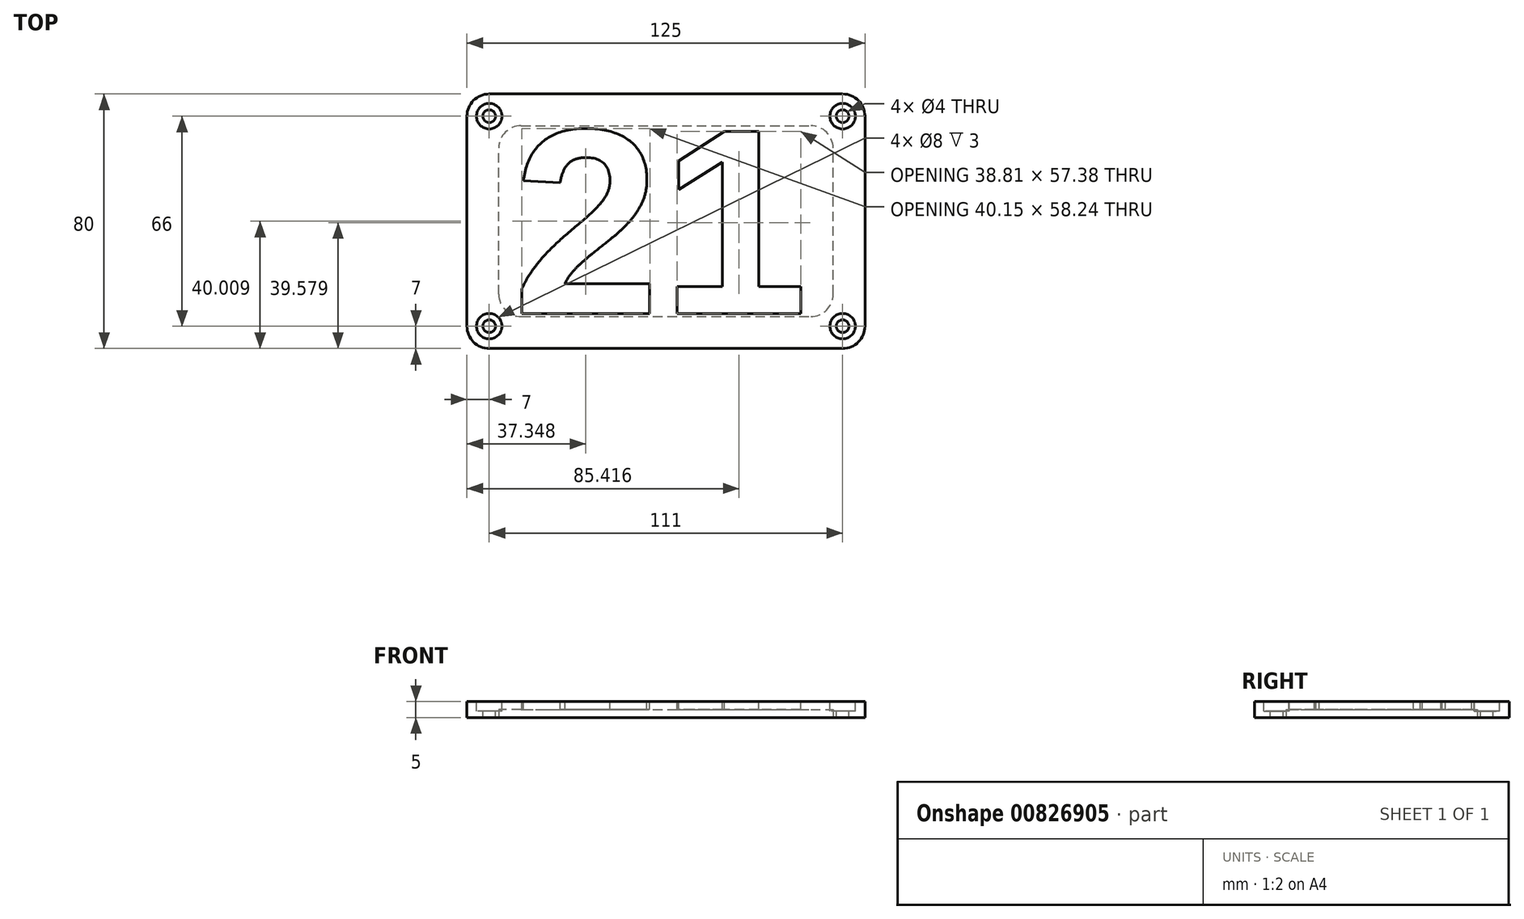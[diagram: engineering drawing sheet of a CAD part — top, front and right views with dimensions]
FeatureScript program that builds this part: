
annotation { "Feature Type Name" : "Feature", "Feature Type Description" : "" }
export const myFeature = defineFeature(function(context is Context, id is Id, definition is map)
    precondition{}
    {
        {
            var Q0;
            Q0=qCreatedBy(makeId("Top.planeOp"),FACE);
            var sketch = newSketch(context, id + "F0", { "sketchPlane" : qUnion([Q0])});
            skLineSegment(sketch, "E0.bottom", {"start": v(-62.5, 40) * mm, "end": v(62.5, 40) * mm});
            skLineSegment(sketch, "E0.top", {"start": v(-62.5, -40) * mm, "end": v(62.5, -40) * mm});
            skLineSegment(sketch, "E0.left", {"start": v(-62.5, 40) * mm, "end": v(-62.5, -40) * mm});
            skLineSegment(sketch, "E0.right", {"start": v(62.5, 40) * mm, "end": v(62.5, -40) * mm});
            skPoint(sketch, "E0.middle", {"position": v(0, 0) * mm});
            skSolve(sketch);
        }
        {
            var Q0;
            Q0=makeQuery(id+"F0.imprint","IMPRINT",FACE,{"disambiguationData":[TD([[makeQuery(id+"F0.imprint","IMPRINT",EDGE,{"derivedFrom":sQuery(id+"F0.wireOp",EDGE,"E0.bottom")}),-1.0]])]});
            extrude(context, id + "F1", {"entities" : qUnion([Q0]), "depth" : 5 * mm, "offsetDistance" : 25.4 * mm});
        }
        {
            var Q0;
            Q0=makeQuery(id+"F1.opExtrude","CAP_FACE",FACE,{"disambiguationData":[OSD([sQuery(id+"F0.wireOp",EDGE,"E0.bottom"),sQuery(id+"F0.wireOp",EDGE,"E0.top"),sQuery(id+"F0.wireOp",EDGE,"E0.left"),sQuery(id+"F0.wireOp",EDGE,"E0.right")])],"isStart":true});
            var sketch = newSketch(context, id + "F2", { "sketchPlane" : qUnion([Q0])});
            skLineSegment(sketch, "E1.bottom", {"start": v(-52.5, 30) * mm, "end": v(52.5, 30) * mm});
            skLineSegment(sketch, "E1.top", {"start": v(-52.5, -30) * mm, "end": v(52.5, -30) * mm});
            skLineSegment(sketch, "E1.left", {"start": v(-52.5, 30) * mm, "end": v(-52.5, -30) * mm});
            skLineSegment(sketch, "E1.right", {"start": v(52.5, 30) * mm, "end": v(52.5, -30) * mm});
            skPoint(sketch, "E1.middle", {"position": v(0, 0) * mm});
            skSolve(sketch);
        }
        {
            var Q0;
            Q0=makeQuery(id+"F2.imprint","IMPRINT",FACE,{"disambiguationData":[TD([[makeQuery(id+"F2.imprint","IMPRINT",EDGE,{"derivedFrom":sQuery(id+"F2.wireOp",EDGE,"E1.bottom")}),-1.0]])]});
            extrude(context, id + "F3", {"entities" : qUnion([Q0]), "operationType" : NewBodyOperationType.REMOVE, "oppositeDirection" : true, "depth" : 2.5 * mm, "offsetDistance" : 25.4 * mm});
        }
        {
            var Q0;
            Q0=makeQuery(id+"F1.opExtrude","SWEPT_EDGE",EDGE,{"disambiguationData":[OSD([sQuery(id+"F0.wireOp",EDGE,"E0.top"),sQuery(id+"F0.wireOp",EDGE,"E0.left")])]});
            var Q1;
            Q1=makeQuery(id+"F1.opExtrude","SWEPT_EDGE",EDGE,{"disambiguationData":[OSD([sQuery(id+"F0.wireOp",EDGE,"E0.top"),sQuery(id+"F0.wireOp",EDGE,"E0.right")])]});
            var Q2;
            Q2=makeQuery(id+"F1.opExtrude","SWEPT_EDGE",EDGE,{"disambiguationData":[OSD([sQuery(id+"F0.wireOp",EDGE,"E0.bottom"),sQuery(id+"F0.wireOp",EDGE,"E0.right")])]});
            var Q3;
            Q3=makeQuery(id+"F1.opExtrude","SWEPT_EDGE",EDGE,{"disambiguationData":[OSD([sQuery(id+"F0.wireOp",EDGE,"E0.bottom"),sQuery(id+"F0.wireOp",EDGE,"E0.left")])]});
            fillet(context, id + "F4", {"entities" : qUnion([Q0, Q1, Q2, Q3]), "radius" : 7 * mm, "tangentPropagation" : true, "allowEdgeOverflow" : false});
        }
        {
            var Q0;
            Q0=makeQuery(id+"F3.boolean.opBoolean","COPY",EDGE,{"derivedFrom":makeQuery(id+"F3.opExtrude","SWEPT_EDGE",EDGE,{"disambiguationData":[OSD([sQuery(id+"F2.wireOp",EDGE,"E1.top"),sQuery(id+"F2.wireOp",EDGE,"E1.left")])]})});
            var Q1;
            Q1=makeQuery(id+"F3.boolean.opBoolean","COPY",EDGE,{"derivedFrom":makeQuery(id+"F3.opExtrude","SWEPT_EDGE",EDGE,{"disambiguationData":[OSD([sQuery(id+"F2.wireOp",EDGE,"E1.top"),sQuery(id+"F2.wireOp",EDGE,"E1.right")])]})});
            var Q2;
            Q2=makeQuery(id+"F3.boolean.opBoolean","COPY",EDGE,{"derivedFrom":makeQuery(id+"F3.opExtrude","SWEPT_EDGE",EDGE,{"disambiguationData":[OSD([sQuery(id+"F2.wireOp",EDGE,"E1.bottom"),sQuery(id+"F2.wireOp",EDGE,"E1.right")])]})});
            var Q3;
            Q3=makeQuery(id+"F3.boolean.opBoolean","COPY",EDGE,{"derivedFrom":makeQuery(id+"F3.opExtrude","SWEPT_EDGE",EDGE,{"disambiguationData":[OSD([sQuery(id+"F2.wireOp",EDGE,"E1.bottom"),sQuery(id+"F2.wireOp",EDGE,"E1.left")])]})});
            fillet(context, id + "F5", {"entities" : qUnion([Q0, Q1, Q2, Q3]), "radius" : 7 * mm, "tangentPropagation" : true, "allowEdgeOverflow" : false});
        }
        {
            var Q0;
            Q0=makeQuery(id+"F1.opExtrude","CAP_FACE",FACE,{"disambiguationData":[OSD([sQuery(id+"F0.wireOp",EDGE,"E0.bottom"),sQuery(id+"F0.wireOp",EDGE,"E0.top"),sQuery(id+"F0.wireOp",EDGE,"E0.left"),sQuery(id+"F0.wireOp",EDGE,"E0.right")])],"isStart":false});
            var sketch = newSketch(context, id + "F6", { "sketchPlane" : qUnion([Q0])});
            skPoint(sketch, "E2", {"position": v(-55.5, -33) * mm});
            skPoint(sketch, "E3", {"position": v(-55.5, 33) * mm});
            skPoint(sketch, "E4", {"position": v(55.5, 33) * mm});
            skPoint(sketch, "E5", {"position": v(55.5, -33) * mm});
            skSolve(sketch);
        }
        {
            var Q0;
            Q0=sQuery(id+"F6.wireOp",VERTEX,"E3");
            var Q1;
            Q1=sQuery(id+"F6.wireOp",VERTEX,"E2");
            var Q2;
            Q2=sQuery(id+"F6.wireOp",VERTEX,"E4");
            var Q3;
            Q3=sQuery(id+"F6.wireOp",VERTEX,"E5");
            var Q4;
            Q4=makeQuery(id+"F1.opExtrude","SWEPT_BODY",BODY,{"disambiguationData":[OSD([sQuery(id+"F0.wireOp",EDGE,"E0.bottom"),sQuery(id+"F0.wireOp",EDGE,"E0.top"),sQuery(id+"F0.wireOp",EDGE,"E0.left"),sQuery(id+"F0.wireOp",EDGE,"E0.right")])]});
            hole(context, id + "F7", {"style" : HoleStyle.C_BORE, "endStyle" : HoleEndStyle.THROUGH, "holeDiameter" : 4 * mm, "cBoreDiameter" : 8 * mm, "cBoreDepth" : 3 * mm, "majorDiameter" : 5 * mm, "isTappedThrough" : true, "tappedDepth" : 12 * mm, "tapClearance" : 3, "locations" : qUnion([Q0, Q1, Q2, Q3]), "scope" : qUnion([Q4])});
        }
        {
            var Q0;
            Q0=makeQuery(id+"F1.opExtrude","CAP_FACE",FACE,{"disambiguationData":[OSD([sQuery(id+"F0.wireOp",EDGE,"E0.bottom"),sQuery(id+"F0.wireOp",EDGE,"E0.top"),sQuery(id+"F0.wireOp",EDGE,"E0.left"),sQuery(id+"F0.wireOp",EDGE,"E0.right")])],"isStart":false});
            var sketch = newSketch(context, id + "F8", { "sketchPlane" : qUnion([Q0])});
            skText(sketch, "E6", { "text": "21", "fontName": "Arimo-Bold.ttf"});
            const initialGuessF8  = {"E6": [-0.04812, -0.02911, 1, 0, 0.06005]};
            skSetInitialGuess(sketch, initialGuessF8);
            skSolve(sketch);
        }
        {
            var Q0;
            Q0=makeQuery(id+"F8.imprint","IMPRINT",FACE,{"disambiguationData":[TD([[makeQuery(id+"F8.imprint","IMPRINT",EDGE,{"derivedFrom":sQuery(id+"F8.wireOp",EDGE,"E6.sketch_text.stroke-0")}),-1.0]])]});
            var Q1;
            Q1=makeQuery(id+"F8.imprint","IMPRINT",FACE,{"disambiguationData":[TD([[makeQuery(id+"F8.imprint","IMPRINT",EDGE,{"derivedFrom":sQuery(id+"F8.wireOp",EDGE,"E6.sketch_text.stroke-22")}),-1.0]])]});
            extrude(context, id + "F9", {"entities" : qUnion([Q0, Q1]), "operationType" : NewBodyOperationType.REMOVE, "endBound" : BoundingType.THROUGH_ALL, "oppositeDirection" : true, "depth" : 25 * mm, "offsetDistance" : 25 * mm});
        }
    });
